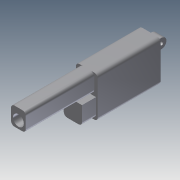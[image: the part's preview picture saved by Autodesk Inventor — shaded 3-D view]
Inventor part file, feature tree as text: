
AUTODESK INVENTOR PART (.ipt)
format: ipt  version: 2011 (Build 150239000, 239)  size: 246,784 bytes
history: native  units: in
note: dims shown in document units (in); Inventor stores cm internally (conversion verified against a paired STEP export)
features: extrude x15, sketch x15, fillet x1
ambient origin geometry x8: Origin, YZ Plane, XZ Plane, XY Plane, X Axis, Y Axis, Z Axis, Center Point
bodies: Solid1 (feature_tree)
feature tree (31):
  extrude  "Extrusion1"  Depth=2.91in
  extrude  "Extrusion2"  Depth=1.56in
  extrude  "Extrusion3"  Depth=0.25in
  extrude  "Extrusion4"  Depth=6.4in TaperAngle=0.0deg
  extrude  "Extrusion5"  Depth=8.0in TaperAngle=0.0deg
  extrude  "Extrusion6"  Depth=1.31in
  extrude  "Extrusion7"  Depth=1.0in TaperAngle=0.0deg
  extrude  "Extrusion8"  Depth=0.7in
  extrude  "Extrusion9"  Depth=0.25in
  extrude  "Extrusion10"  Depth=0.7in TaperAngle=0.0deg
  fillet  "Fillet1"  Radius=1.5in
  extrude  "Extrusion11"  Depth=0.78in
  extrude  "Extrusion12"  Depth=9.0in TaperAngle=0.0deg
  extrude  "Extrusion13"  Depth=8.0in TaperAngle=0.0deg
  extrude  "Extrusion14"  [1 undecoded]
  extrude  "Extrusion15"  [1 undecoded]
  sketch  "Sketch1"  dims[d0=1.56in d1=2.91in]
  sketch  "Sketch2"  dims[d2=3.0in d3=0.0in d4=1.56in]
  sketch  "Sketch3"  dims[d5=0.25in d6=0.25in]
  sketch  "Sketch4"  dims[d7=1.06in d8=6.4in d9=0.0in]
  sketch  "Sketch5"  dims[d10=0.78in d11=8.0in d12=0.0in]
  sketch  "Sketch6"  dims[d13=1.0in d14=0.0in d15=1.31in]
  sketch  "Sketch7"  dims[d16=3.5in d17=0.0in d18=1.0in d19=0.0in]
  sketch  "Sketch8"  dims[d20=45.0deg d21=0.7in]
  sketch  "Sketch9"  dims[d22=0.5in d23=0.0in d24=0.25in]
  sketch  "Sketch10"  dims[d25=1.0in d26=0.0in d27=0.7in d28=0.0in d29=1.5in d30=0.0in]
  sketch  "Sketch11"  dims[d31=0.25in d32=0.78in]
  sketch  "Sketch12"  dims[d33=4.0in d34=0.0in d35=9.0in d36=0.0in]
  sketch  "Sketch13"  dims[d37=4.0in d38=0.0in d39=8.0in d40=0.0in]
  sketch  "Sketch14"  dims[d41=8.0in d42=0.0in]
  sketch  "Sketch15"
note: 2 required parameter values undecoded (feature->parameter linkage not recoverable at this tier; creation-order binding heuristic only, values carry confidence <= 0.55)
